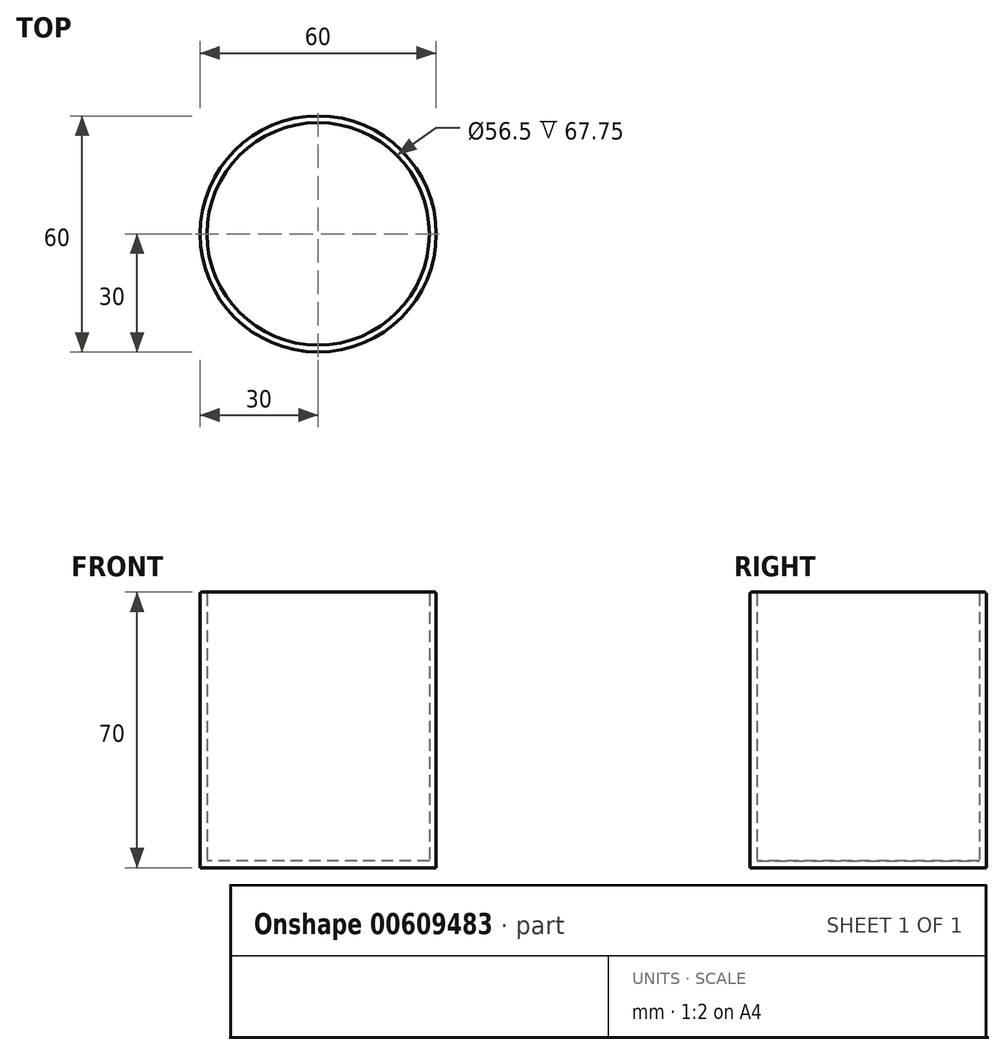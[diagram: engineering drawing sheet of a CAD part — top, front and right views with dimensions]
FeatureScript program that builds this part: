
annotation { "Feature Type Name" : "Feature", "Feature Type Description" : "" }
export const myFeature = defineFeature(function(context is Context, id is Id, definition is map)
    precondition{}
    {
        {
            var Q0;
            Q0=qCreatedBy(makeId("Top.planeOp"),FACE);
            var sketch = newSketch(context, id + "F0", { "sketchPlane" : qUnion([Q0])});
            skCircle(sketch, "E0", {"center": v(0, 0) * mm, "radius": 30 * mm});
            skSolve(sketch);
        }
        {
            var Q0;
            Q0=makeQuery(id+"F0.imprint","IMPRINT",FACE,{"disambiguationData":[TD([[makeQuery(id+"F0.imprint","IMPRINT",EDGE,{"derivedFrom":sQuery(id+"F0.wireOp",EDGE,"E0")}),1.0]])]});
            extrude(context, id + "F1", {"entities" : qUnion([Q0]), "depth" : 70 * mm, "offsetDistance" : 25 * mm});
        }
        {
            var Q0;
            Q0=makeQuery(id+"F1.opExtrude","CAP_FACE",FACE,{"disambiguationData":[OSD([sQuery(id+"F0.wireOp",EDGE,"E0")])],"isStart":false});
            shell(context, id + "F2", {"entities" : qUnion([Q0]), "thickness" : 1.75 * mm});
        }
        {
            var Q0;
            Q0=makeQuery(id+"F1.opExtrude","CAP_EDGE",EDGE,{"disambiguationData":[OSD([sQuery(id+"F0.wireOp",EDGE,"E0")])],"isStart":false});
            var Q1;
            {var subQ0=sQuery(id+"F0.wireOp",EDGE,"E0");Q1=makeQuery(id+"F2.opShell","OFFSET_EDGE",EDGE,{"disambiguationData":[OSD([subQ0]),TDD([makeQuery(id+"F1.opExtrude","CAP_EDGE",EDGE,{"disambiguationData":[OSD([subQ0])],"isStart":false})])]});}
            fillet(context, id + "F3", {"entities" : qUnion([Q0, Q1]), "radius" : 0.5 * mm, "tangentPropagation" : true, "allowEdgeOverflow" : false});
        }
    });
